# Revit family: Poly Max - Ceiling and Wall Panels
name_source: partatom
category: Generic Models
revit_build: Autodesk Revit 2016 (Build: 20150220_1215(x64)
units: mm (PartAtom-declared; Revit-internal decimal feet)

## family parameters
Always vertical = No
Can host rebar = No
Cut with Voids When Loaded = No
Part Type = Normal
Room Calculation Point = No
Round Connector Dimension = Use Diameter
Shared = No
Work Plane-Based = Yes

## types (46) — shared parameters
A = 0' - 0"
Default Elevation = 4' - 0"
Manufacturer = Acoustical Surfaces, Inc.
Material = Poly Max
URL = https://www.acousticalsurfaces.com

## per-type parameters (varying)
| type | Finish | Length | T | Thickness Options | Width | ‍      0. Thickness 1/2" | ‍      1. Thickness 1" | ‍      2. Thickness 2" |
| HALF INCH THICK - 48X96 - Printed Grpahics | Poly Max - Printed Graphics | 8' - 0" | 0' - 0 1/2" | 0 | 4' - 0" | Yes | No | No |
| HALF INCH THICK - 48X96 - Lime | Poly Max - Lime | 8' - 0" | 0' - 0 1/2" | 0 | 4' - 0" | Yes | No | No |
| HALF INCH THICK - 48X96 - Orange | Poly Max - Orange | 8' - 0" | 0' - 0 1/2" | 0 | 4' - 0" | Yes | No | No |
| HALF INCH THICK - 48X96 - Red | Poly Max - Red | 8' - 0" | 0' - 0 1/2" | 0 | 4' - 0" | Yes | No | No |
| HALF INCH THICK - 48X96 - Purple | Poly Max - Purple | 8' - 0" | 0' - 0 1/2" | 0 | 4' - 0" | Yes | No | No |
| HALF INCH THICK - 48X96 - Blue | Poly Max - Blue | 8' - 0" | 0' - 0 1/2" | 0 | 4' - 0" | Yes | No | No |
| HALF INCH THICK - 48X96 - Black | Poly Max - Black | 8' - 0" | 0' - 0 1/2" | 0 | 4' - 0" | Yes | No | No |
| HALF INCH THICK - 48X96 - Grey | Poly Max - Grey | 8' - 0" | 0' - 0 1/2" | 0 | 4' - 0" | Yes | No | No |
| HALF INCH THICK - 48X96 - Silver | Poly Max - Silver | 8' - 0" | 0' - 0 1/2" | 0 | 4' - 0" | Yes | No | No |
| HALF INCH THICK - 48X96 - Brown | Poly Max - Brown | 8' - 0" | 0' - 0 1/2" | 0 | 4' - 0" | Yes | No | No |
| HALF INCH THICK - 48X96 - Tan | Poly Max - Tan | 8' - 0" | 0' - 0 1/2" | 0 | 4' - 0" | Yes | No | No |
| HALF INCH THICK - 48X96 - Beige | Poly Max - Beige | 8' - 0" | 0' - 0 1/2" | 0 | 4' - 0" | Yes | No | No |
| HALF INCH THICK - 48X96 - White | Poly Max - White | 8' - 0" | 0' - 0 1/2" | 0 | 4' - 0" | Yes | No | No |
| HALF INCH THICK - 24x48 - Tan | Poly Max - Tan | 4' - 0" | 0' - 0 1/2" | 0 | 2' - 0" | Yes | No | No |
| HALF INCH THICK - 24x48 - Brown | Poly Max - Brown | 4' - 0" | 0' - 0 1/2" | 0 | 2' - 0" | Yes | No | No |
| HALF INCH THICK - 24x48 - Grey | Poly Max - Grey | 4' - 0" | 0' - 0 1/2" | 0 | 2' - 0" | Yes | No | No |
| HALF INCH THICK - 24x48 - Blue | Poly Max - Blue | 4' - 0" | 0' - 0 1/2" | 0 | 2' - 0" | Yes | No | No |
| HALF INCH THICK - 24x48 - Purple | Poly Max - Purple | 4' - 0" | 0' - 0 1/2" | 0 | 2' - 0" | Yes | No | No |
| HALF INCH THICK - 24x48 - Red | Poly Max - Red | 4' - 0" | 0' - 0 1/2" | 0 | 2' - 0" | Yes | No | No |
| HALF INCH THICK - 24x48 - Orange | Poly Max - Orange | 4' - 0" | 0' - 0 1/2" | 0 | 2' - 0" | Yes | No | No |
| HALF INCH THICK - 24x48 Lime | Poly Max - Lime | 4' - 0" | 0' - 0 1/2" | 0 | 2' - 0" | Yes | No | No |
| HALF INCH THICK - 24x48 - Printed Graphics | Poly Max - Printed Graphics | 4' - 0" | 0' - 0 1/2" | 0 | 2' - 0" | Yes | No | No |
| HALF INCH THICK - 24x48 - Black | Poly Max - Black | 4' - 0" | 0' - 0 1/2" | 0 | 2' - 0" | Yes | No | No |
| HALF INCH THICK - 24x48 - Silver | Poly Max - Silver | 4' - 0" | 0' - 0 1/2" | 0 | 2' - 0" | Yes | No | No |
| HALF INCH THICK - 24x48 - Beige | Poly Max - Beige | 4' - 0" | 0' - 0 1/2" | 0 | 2' - 0" | Yes | No | No |
| HALF INCH THICK - 24x48 -White | Poly Max - White | 4' - 0" | 0' - 0 1/2" | 0 | 2' - 0" | Yes | No | No |
| 1 INCH THICK - 48X96 - Printed Graphics | Poly Max - Printed Graphics | 8' - 0" | 0' - 1" | 1 | 4' - 0" | No | Yes | No |
| 1 INCH THICK - 48X96 - Silver | Poly Max - Silver | 8' - 0" | 0' - 1" | 1 | 4' - 0" | No | Yes | No |
| 1 INCH THICK - 48X96 - Black | Poly Max - Black | 8' - 0" | 0' - 1" | 1 | 4' - 0" | No | Yes | No |
| 1 INCH THICK - 48X96 Beige | Poly Max - Beige | 8' - 0" | 0' - 1" | 1 | 4' - 0" | No | Yes | No |
| 1 INCH THICK - 48X96 - White | Poly Max - White | 8' - 0" | 0' - 1" | 1 | 4' - 0" | No | Yes | No |
| 2 INCH THICK - 48X96 - Printed Graphics | Poly Max - Printed Graphics | 8' - 0" | 0' - 2" | 2 | 4' - 0" | No | No | Yes |
| 2 INCH THICK - 48X96 - Silver | Poly Max - Silver | 8' - 0" | 0' - 2" | 2 | 4' - 0" | No | No | Yes |
| 2 INCH THICK - 48X96 - Black | Poly Max - Black | 8' - 0" | 0' - 2" | 2 | 4' - 0" | No | No | Yes |
| 2 INCH THICK - 48X96 - Beige | Poly Max - Beige | 8' - 0" | 0' - 2" | 2 | 4' - 0" | No | No | Yes |
| 2 INCH THICK - 48X96 - White | Poly Max - White | 8' - 0" | 0' - 2" | 2 | 4' - 0" | No | No | Yes |
| 2 INCH THICK - 24x48 - Printed Graphics | Poly Max - Printed Graphics | 4' - 0" | 0' - 0 1/2" | 0 | 2' - 0" | Yes | No | No |
| 2 INCH THICK - 24x48 - Silver | Poly Max - Silver | 4' - 0" | 0' - 0 1/2" | 0 | 2' - 0" | Yes | No | No |
| 2 INCH THICK - 24x48 - Black | Poly Max - Black | 4' - 0" | 0' - 0 1/2" | 0 | 2' - 0" | Yes | No | No |
| 2 INCH THICK - 24x48 - White | Poly Max - White | 4' - 0" | 0' - 0 1/2" | 0 | 2' - 0" | Yes | No | No |
| 1 INCH THICK - 24x48 - Silver | Poly Max - Silver | 4' - 0" | 0' - 1" | 1 | 2' - 0" | No | Yes | No |
| 1 INCH THICK - 24x48 - Black | Poly Max - Black | 4' - 0" | 0' - 1" | 1 | 2' - 0" | No | Yes | No |
| 1 INCH THICK - 24x48 - Beige | Poly Max - Beige | 4' - 0" | 0' - 1" | 1 | 2' - 0" | No | Yes | No |
| 1 INCH THICK - 24x48 - White | Poly Max - White | 4' - 0" | 0' - 1" | 1 | 2' - 0" | No | Yes | No |
| 2 INCH THICK - 24x48 - Beige | Poly Max - Beige | 4' - 0" | 0' - 0 1/2" | 0 | 2' - 0" | Yes | No | No |
| 1 INCH THICK - 24x48 - Printed Graphics | Poly Max - Printed Graphics | 4' - 0" | 0' - 1" | 1 | 2' - 0" | No | Yes | No |

## geometry (parser evidence)
native form markers: Sweep x9
no freeform markers — native parametric forms only
